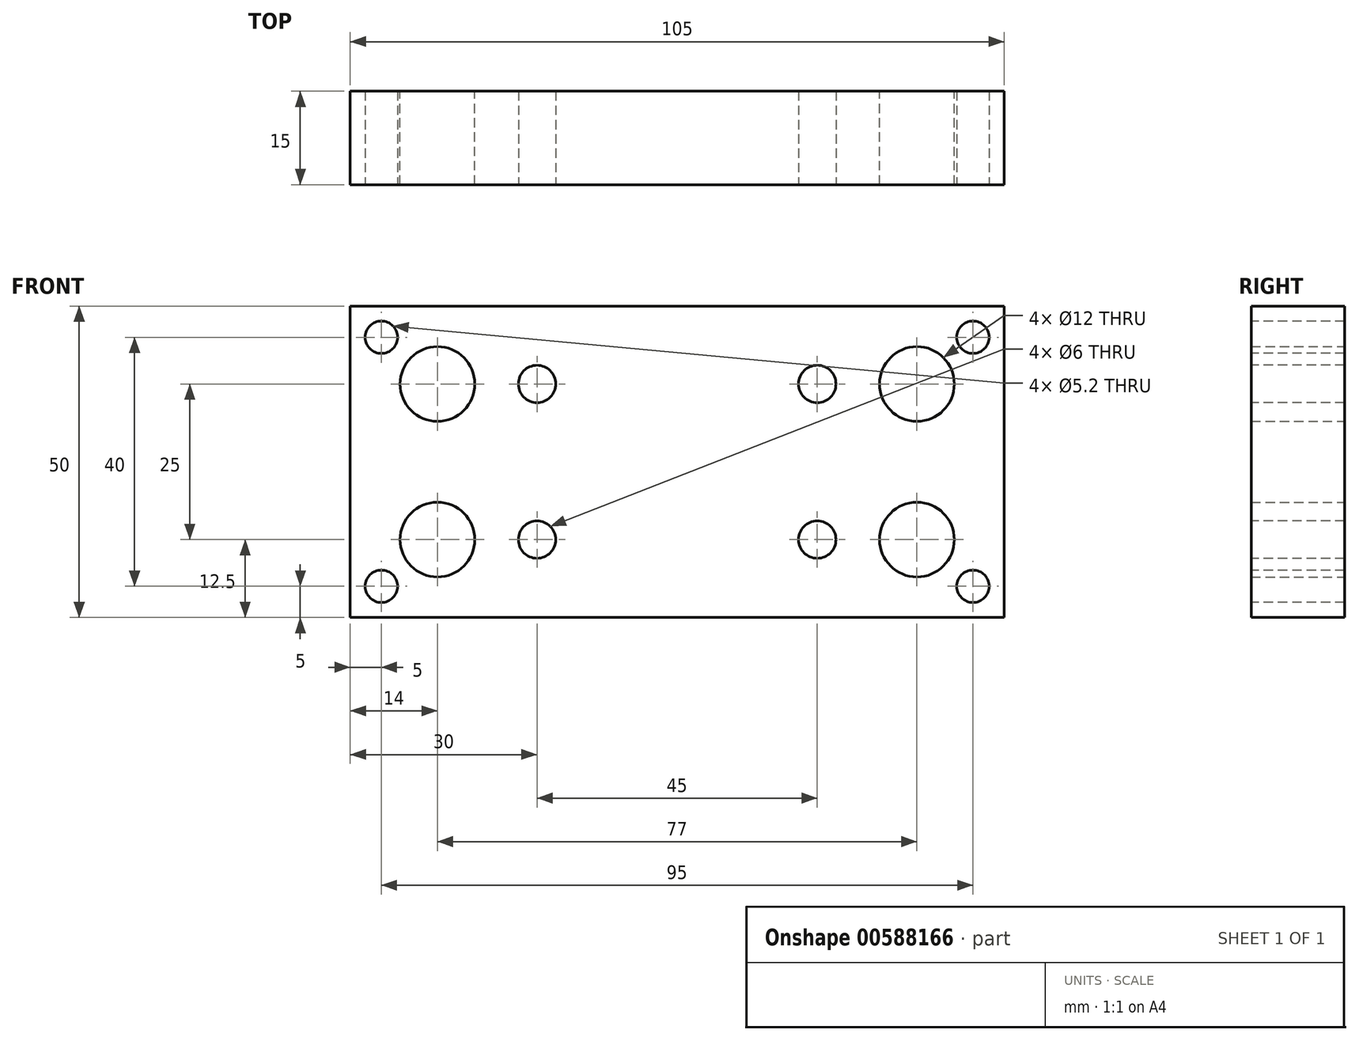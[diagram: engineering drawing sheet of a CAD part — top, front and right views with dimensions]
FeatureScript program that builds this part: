
annotation { "Feature Type Name" : "Feature", "Feature Type Description" : "" }
export const myFeature = defineFeature(function(context is Context, id is Id, definition is map)
    precondition{}
    {
        {
            var Q0;
            Q0=qCreatedBy(makeId("Front.planeOp"),FACE);
            var sketch = newSketch(context, id + "F0", { "sketchPlane" : qUnion([Q0])});
            skLineSegment(sketch, "E0.bottom", {"start": v(0, 0) * mm, "end": v(105, 0) * mm});
            skLineSegment(sketch, "E0.top", {"start": v(0, 50) * mm, "end": v(105, 50) * mm});
            skLineSegment(sketch, "E0.left", {"start": v(0, 0) * mm, "end": v(0, 50) * mm});
            skLineSegment(sketch, "E0.right", {"start": v(105, 0) * mm, "end": v(105, 50) * mm});
            skLineSegment(sketch, "E1.bottom", {"start": v(14, 37.5) * mm, "end": v(91, 37.5) * mm, "construction": true});
            skLineSegment(sketch, "E1.top", {"start": v(14, 12.5) * mm, "end": v(91, 12.5) * mm, "construction": true});
            skLineSegment(sketch, "E1.left", {"start": v(14, 37.5) * mm, "end": v(14, 12.5) * mm, "construction": true});
            skLineSegment(sketch, "E1.right", {"start": v(91, 37.5) * mm, "end": v(91, 12.5) * mm, "construction": true});
            skCircle(sketch, "E2", {"center": v(14, 37.5) * mm, "radius": 6 * mm});
            skCircle(sketch, "E3", {"center": v(91, 37.5) * mm, "radius": 6 * mm});
            skCircle(sketch, "E4", {"center": v(14, 12.5) * mm, "radius": 6 * mm});
            skCircle(sketch, "E5", {"center": v(91, 12.5) * mm, "radius": 6 * mm});
            skSolve(sketch);
        }
        {
            var Q0;
            Q0 = qSketchRegion(id + "F0", true);
            extrude(context, id + "F1", {"entities" : qUnion([Q0]), "depth" : 15 * mm, "offsetDistance" : 25 * mm});
        }
        {
            var Q0;
            Q0=makeQuery(id+"F1.opExtrude","CAP_FACE",FACE,{"disambiguationData":[OSD([sQuery(id+"F0.wireOp",EDGE,"E0.bottom"),sQuery(id+"F0.wireOp",EDGE,"E0.top"),sQuery(id+"F0.wireOp",EDGE,"E0.left"),sQuery(id+"F0.wireOp",EDGE,"E0.right"),sQuery(id+"F0.wireOp",EDGE,"E2"),sQuery(id+"F0.wireOp",EDGE,"E3"),sQuery(id+"F0.wireOp",EDGE,"E4"),sQuery(id+"F0.wireOp",EDGE,"E5")])],"isStart":false});
            var sketch = newSketch(context, id + "F2", { "sketchPlane" : qUnion([Q0])});
            skLineSegment(sketch, "E6", {"start": v(14, 37.5) * mm, "end": v(91, 37.5) * mm, "construction": true});
            skLineSegment(sketch, "E7", {"start": v(91, 12.5) * mm, "end": v(14, 12.5) * mm, "construction": true});
            skLineSegment(sketch, "E8", {"start": v(30, 37.5) * mm, "end": v(30, 12.5) * mm, "construction": true});
            skLineSegment(sketch, "E9", {"start": v(75, 37.5) * mm, "end": v(75, 12.5) * mm, "construction": true});
            skCircle(sketch, "E10", {"center": v(30, 37.5) * mm, "radius": 3 * mm});
            skCircle(sketch, "E11", {"center": v(75, 37.5) * mm, "radius": 3 * mm});
            skCircle(sketch, "E12", {"center": v(30, 12.5) * mm, "radius": 3 * mm});
            skCircle(sketch, "E13", {"center": v(75, 12.5) * mm, "radius": 3 * mm});
            skSolve(sketch);
        }
        {
            var Q0;
            Q0 = qSketchRegion(id + "F2", true);
            extrude(context, id + "F3", {"entities" : qUnion([Q0]), "operationType" : NewBodyOperationType.REMOVE, "endBound" : BoundingType.UP_TO_NEXT, "oppositeDirection" : true, "depth" : 25 * mm, "offsetDistance" : 25 * mm});
        }
        {
            var Q0;
            Q0=makeQuery(id+"F1.opExtrude","CAP_FACE",FACE,{"disambiguationData":[OSD([sQuery(id+"F0.wireOp",EDGE,"E0.bottom"),sQuery(id+"F0.wireOp",EDGE,"E0.top"),sQuery(id+"F0.wireOp",EDGE,"E0.left"),sQuery(id+"F0.wireOp",EDGE,"E0.right"),sQuery(id+"F0.wireOp",EDGE,"E2"),sQuery(id+"F0.wireOp",EDGE,"E3"),sQuery(id+"F0.wireOp",EDGE,"E4"),sQuery(id+"F0.wireOp",EDGE,"E5")])],"isStart":false});
            var sketch = newSketch(context, id + "F4", { "sketchPlane" : qUnion([Q0])});
            skCircle(sketch, "E14", {"center": v(5, 45) * mm, "radius": 2.6 * mm});
            skCircle(sketch, "E15", {"center": v(100, 45) * mm, "radius": 2.6 * mm});
            skCircle(sketch, "E16", {"center": v(100, 5) * mm, "radius": 2.6 * mm});
            skCircle(sketch, "E17", {"center": v(5, 5) * mm, "radius": 2.6 * mm});
            skSolve(sketch);
        }
        {
            var Q0;
            Q0 = qSketchRegion(id + "F4", true);
            extrude(context, id + "F5", {"entities" : qUnion([Q0]), "operationType" : NewBodyOperationType.REMOVE, "endBound" : BoundingType.UP_TO_NEXT, "oppositeDirection" : true, "depth" : 25 * mm, "offsetDistance" : 25 * mm});
        }
    });
